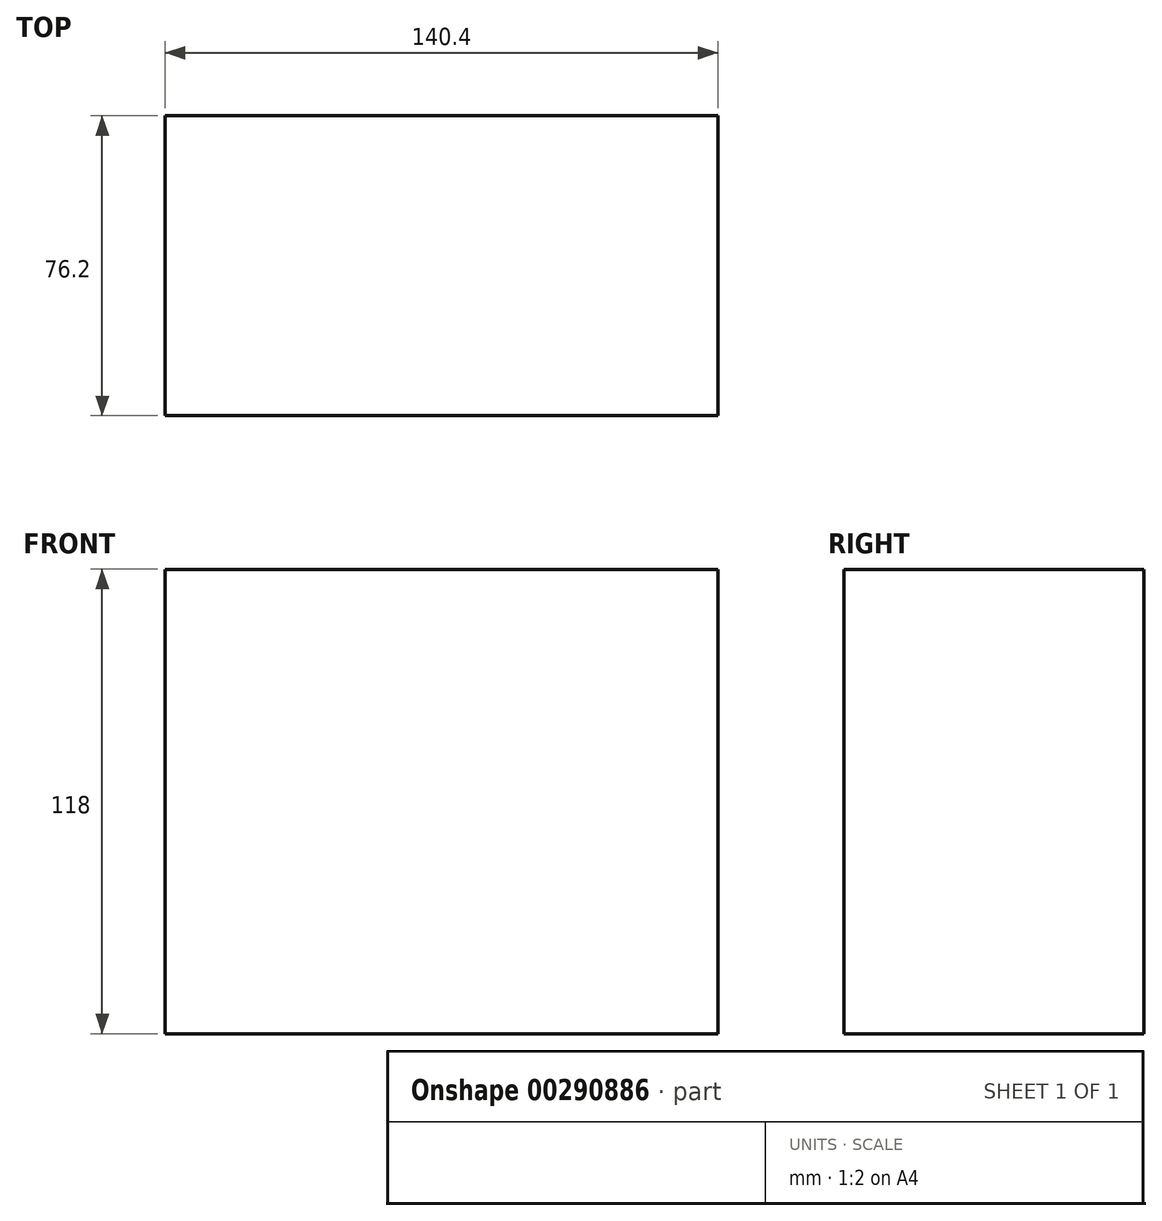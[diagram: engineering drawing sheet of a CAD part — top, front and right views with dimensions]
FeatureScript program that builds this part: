
annotation { "Feature Type Name" : "Feature", "Feature Type Description" : "" }
export const myFeature = defineFeature(function(context is Context, id is Id, definition is map)
    precondition{}
    {
        {
            var Q0;
            Q0=qCreatedBy(makeId("Front.planeOp"),FACE);
            var sketch = newSketch(context, id + "F0", { "sketchPlane" : qUnion([Q0])});
            skLineSegment(sketch, "E0.bottom", {"start": v(70.2, -59) * mm, "end": v(-70.2, -59) * mm});
            skLineSegment(sketch, "E0.top", {"start": v(70.2, 59) * mm, "end": v(-70.2, 59) * mm});
            skLineSegment(sketch, "E0.left", {"start": v(70.2, -59) * mm, "end": v(70.2, 59) * mm});
            skLineSegment(sketch, "E0.right", {"start": v(-70.2, -59) * mm, "end": v(-70.2, 59) * mm});
            skPoint(sketch, "E0.middle", {"position": v(0, 0) * mm});
            skSolve(sketch);
        }
        {
            var Q0;
            Q0 = qSketchRegion(id + "F0", true);
            extrude(context, id + "F1", {"entities" : qUnion([Q0]), "depth" : 76.2 * mm});
        }
    });
